# Revit family: Kühlschrank-Tiefkühlung Einfahr - Eigen
name_source: partatom
category: Sonderausstattung
revit_build: Autodesk Revit 2015 (Build: 20140606_1530(x64)
units: mm (PartAtom-declared; Revit-internal decimal feet)

## types (1)
- BR 710 - 770 x 800 x 2100
    Artikelnr. = HKMTE71-01
    Breite = 770 mm  [stored 2.52625 ft]
    Dichtung Stärke = 20 mm  [stored 0.0656168 ft]
    Elektroanschluss Abstand Seite = 250 mm  [stored 0.82021 ft]
    Elektroanschluss Höhe = 1900 mm  [stored 6.2336 ft]
    Energieeffizienzklasse = F
    Energieverbrauch = 7,8 kWh/24h
    Füße Abstand Hinten = 55 mm  [stored 0.180446 ft]
    Füße Abstand Seiten = 55 mm  [stored 0.180446 ft]
    Füße Abstand Vorne = 55 mm  [stored 0.180446 ft]
    Hersteller = CoolCompact
    Kapazität = 720 l
    Kopfteil Höhe = 300 mm
    Kopfteil Tiefe = 60 mm  [stored 0.19685 ft]
    Kopfteil Verlängerung = 0 mm  [stored 0 ft]
    Korpus Höhe = 1800 mm  [stored 5.90551 ft]
    Korpus Tiefe = 740 mm  [stored 2.42782 ft]
    Kälteleistung = 560W bei -30°C VT/+32°C UT
    Kältemittel = R290
    Material = Edelstahl AISI 304
    Netzkabellänge = 2500 mm  [stored 8.2021 ft]
    Pole = 1
    Scheinleistung = 0 VA
    Sockelhöhe = 0 mm  [stored 0 ft]
    Spannung = 230 V
    Temp. Bereich = -15°C bis -22°C
    Türabstand Links = 5 mm  [stored 0.0164042 ft]
    Türabstand Oben = 10 mm  [stored 0.0328084 ft]
    Türabstand Rechts = 5 mm  [stored 0.0164042 ft]
    Türabstand Unten = 5 mm  [stored 0.0164042 ft]
    Türen Anzahl = 1
    Türen Breite = 760 mm
    Türen Höhe = 1785 mm
    Türen Stärke = 40 mm  [stored 0.131234 ft]
    Wandstärke Hinten = 60 mm  [stored 0.19685 ft]
    Wandstärke Oben = 85 mm  [stored 0.278871 ft]
    Wandstärke Seiten = 80 mm  [stored 0.262467 ft]
    Watt = 450 W

note: [stored X ft] marks values corroborated as IEEE doubles in the binary element streams (Revit-internal decimal feet)

## geometry (parser evidence)
native form markers: Blend x26, Sweep x3
no freeform markers — native parametric forms only
